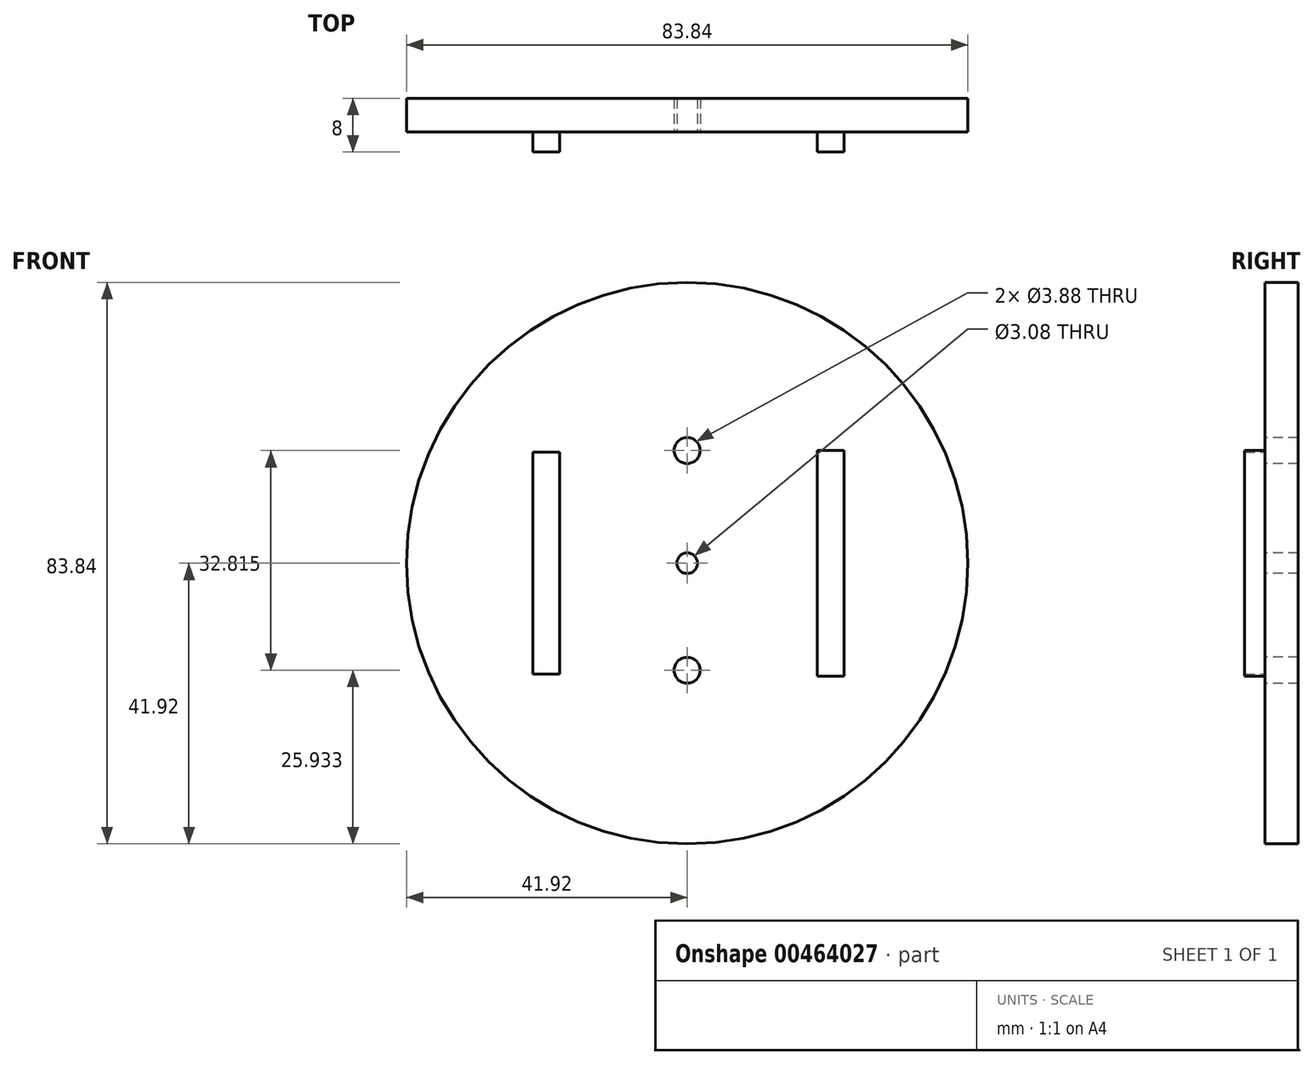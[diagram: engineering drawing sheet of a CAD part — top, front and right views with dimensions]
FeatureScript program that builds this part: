
annotation { "Feature Type Name" : "Feature", "Feature Type Description" : "" }
export const myFeature = defineFeature(function(context is Context, id is Id, definition is map)
    precondition{}
    {
        {
            var Q0;
            Q0=qCreatedBy(makeId("Front.planeOp"),FACE);
            var sketch = newSketch(context, id + "F0", { "sketchPlane" : qUnion([Q0])});
            skCircle(sketch, "E0", {"center": v(0, 0) * mm, "radius": 41.92 * mm});
            skSolve(sketch);
        }
        {
            var Q0;
            Q0=makeQuery(id+"F0.imprint","IMPRINT",FACE,{"disambiguationData":[TD([[makeQuery(id+"F0.imprint","IMPRINT",EDGE,{"derivedFrom":sQuery(id+"F0.wireOp",EDGE,"E0")}),1.0]])]});
            extrude(context, id + "F1", {"entities" : qUnion([Q0]), "oppositeDirection" : true, "depth" : 5 * mm});
        }
        {
            var Q0;
            Q0=qCreatedBy(makeId("Front.planeOp"),FACE);
            var sketch = newSketch(context, id + "F2", { "sketchPlane" : qUnion([Q0])});
            skCircle(sketch, "E1", {"center": v(0, 16.83) * mm, "radius": 1.94 * mm});
            skCircle(sketch, "E2", {"center": v(0, -15.99) * mm, "radius": 1.94 * mm});
            skCircle(sketch, "E3", {"center": v(0, 0) * mm, "radius": 1.54 * mm});
            skSolve(sketch);
        }
        {
            var Q0;
            Q0=qSketchRegion(id+"F2",true);
            extrude(context, id + "F3", {"entities" : qUnion([Q0]), "operationType" : NewBodyOperationType.REMOVE, "oppositeDirection" : true, "depth" : 50.7 * mm});
        }
        {
            var Q0;
            Q0=qCreatedBy(makeId("Front.planeOp"),FACE);
            var sketch = newSketch(context, id + "F4", { "sketchPlane" : qUnion([Q0])});
            skLineSegment(sketch, "E4.bottom", {"start": v(23.43, 16.86) * mm, "end": v(19.43, 16.86) * mm});
            skLineSegment(sketch, "E4.top", {"start": v(23.43, -16.86) * mm, "end": v(19.43, -16.86) * mm});
            skLineSegment(sketch, "E4.left", {"start": v(23.43, 16.86) * mm, "end": v(23.43, -16.86) * mm});
            skLineSegment(sketch, "E4.right", {"start": v(19.43, 16.86) * mm, "end": v(19.43, -16.86) * mm});
            skPoint(sketch, "E4.middle", {"position": v(21.43, 0) * mm});
            skLineSegment(sketch, "E5.bottom", {"start": v(-19.02, 16.58) * mm, "end": v(-23.02, 16.58) * mm});
            skLineSegment(sketch, "E5.top", {"start": v(-19.02, -16.58) * mm, "end": v(-23.02, -16.58) * mm});
            skLineSegment(sketch, "E5.left", {"start": v(-19.02, 16.58) * mm, "end": v(-19.02, -16.58) * mm});
            skLineSegment(sketch, "E5.right", {"start": v(-23.02, 16.58) * mm, "end": v(-23.02, -16.58) * mm});
            skPoint(sketch, "E5.middle", {"position": v(-21.02, 0) * mm});
            skSolve(sketch);
        }
        {
            var Q0;
            Q0=qCreatedBy(makeId("Front.planeOp"),FACE);
            var sketch = newSketch(context, id + "F5", { "sketchPlane" : qUnion([Q0])});
            skSolve(sketch);
        }
        {
            var Q0;
            Q0=qSketchRegion(id+"F5",true);
            var Q1;
            Q1=makeQuery(id+"F4.imprint","IMPRINT",FACE,{"disambiguationData":[TD([[makeQuery(id+"F4.imprint","IMPRINT",EDGE,{"derivedFrom":sQuery(id+"F4.wireOp",EDGE,"E5.bottom")}),1.0]])]});
            var Q2;
            Q2=makeQuery(id+"F4.imprint","IMPRINT",FACE,{"disambiguationData":[TD([[makeQuery(id+"F4.imprint","IMPRINT",EDGE,{"derivedFrom":sQuery(id+"F4.wireOp",EDGE,"E4.bottom")}),1.0]])]});
            extrude(context, id + "F6", {"entities" : qUnion([Q0, Q1, Q2]), "operationType" : NewBodyOperationType.ADD, "depth" : 3 * mm});
        }
    });
